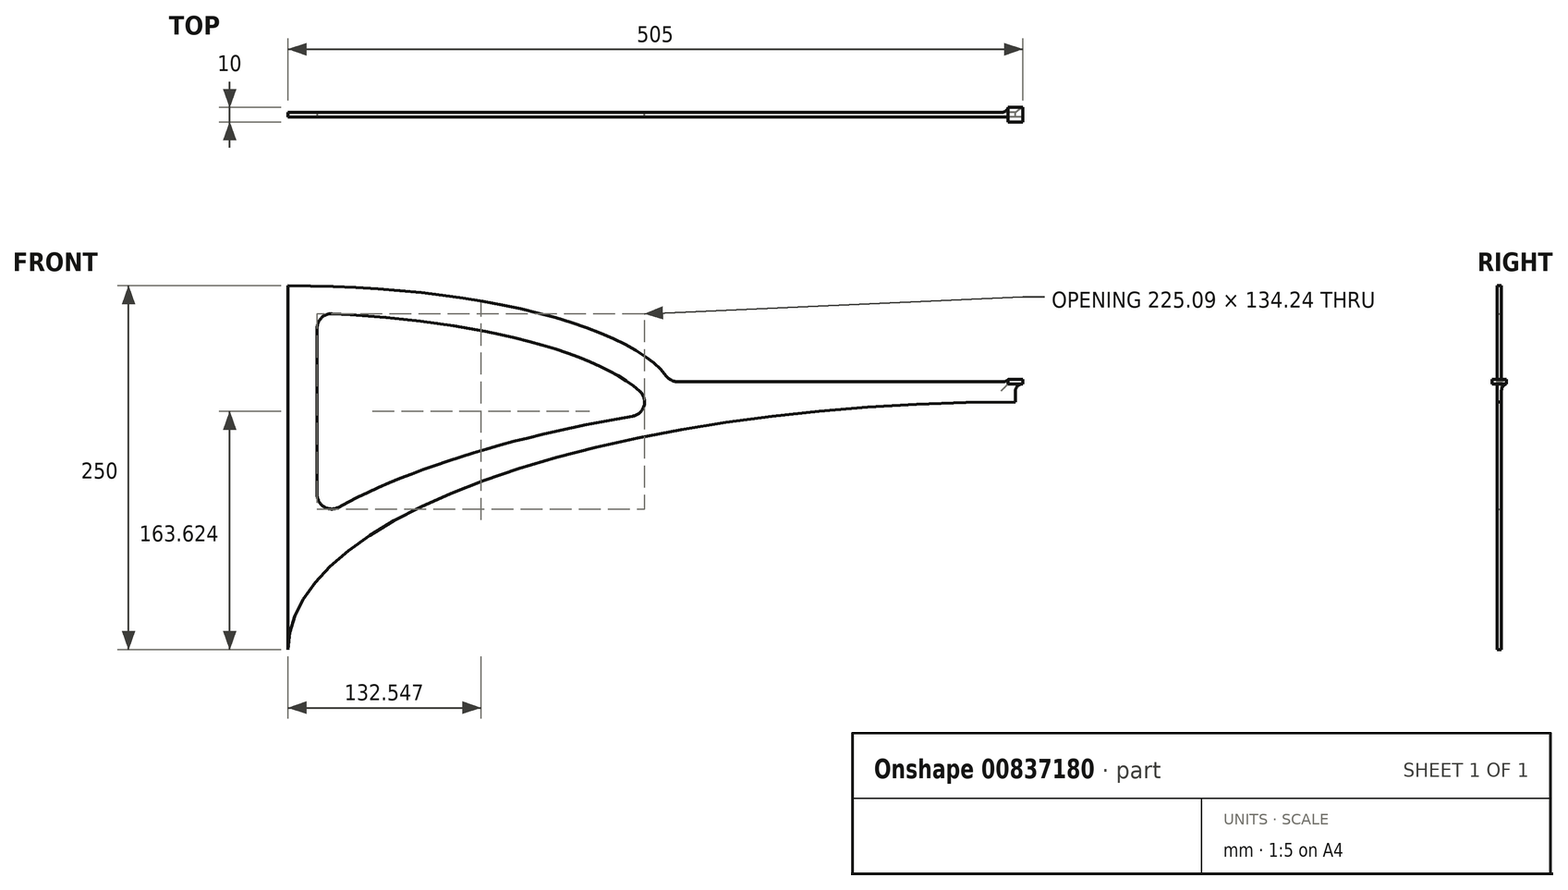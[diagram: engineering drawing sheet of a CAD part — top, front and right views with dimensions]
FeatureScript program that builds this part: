
annotation { "Feature Type Name" : "Feature", "Feature Type Description" : "" }
export const myFeature = defineFeature(function(context is Context, id is Id, definition is map)
    precondition{}
    {
        {
            var Q0;
            Q0=qCreatedBy(makeId("Front.planeOp"),FACE);
            var sketch = newSketch(context, id + "F0", { "sketchPlane" : qUnion([Q0])});
            skLineSegment(sketch, "E0", {"start": v(0, 0) * mm, "end": v(20, 0) * mm});
            skLineSegment(sketch, "E1", {"start": v(0, 0) * mm, "end": v(0, -170) * mm});
            skLineSegment(sketch, "E2", {"start": v(0, 0) * mm, "end": v(0, 80) * mm});
            skEllipticalArc(sketch, "E3", {});
            skEllipticalArc(sketch, "E4", {});
            skLineSegment(sketch, "E5", {"start": v(0, 80) * mm, "end": v(20, 80) * mm});
            skLineSegment(sketch, "E6", {"start": v(20, 80) * mm, "end": v(20, 79.77) * mm});
            skEllipticalArc(sketch, "E7", {});
            skEllipticalArc(sketch, "E8.trimOffspring", {});
            skLineSegment(sketch, "E9.trimOffspring", {"start": v(20, 61.17) * mm, "end": v(20, -80.93) * mm});
            skLineSegment(sketch, "E10", {"start": v(495, 14) * mm, "end": v(262.66, 14) * mm});
            skLineSegment(sketch, "E11", {"start": v(500, 12.5) * mm, "end": v(500, 0) * mm});
            skLineSegment(sketch, "E12", {"start": v(505, 15.5) * mm, "end": v(505, 12.5) * mm});
            skLineSegment(sketch, "E13", {"start": v(505, 12.5) * mm, "end": v(495, 12.5) * mm});
            skLineSegment(sketch, "E14", {"start": v(495, 12.5) * mm, "end": v(495, 15.5) * mm});
            skLineSegment(sketch, "E15", {"start": v(505, 15.5) * mm, "end": v(495, 15.5) * mm});
            const initialGuessF0  = {"E3": [0.5, -0.17, -1, 0, 0.5, 0.17, 4.71238898038469, 0], "E4": [0, 0, 1, 0, 0.2667732536792755, 0.08, 0.175905768163716, 1.5707963267948966], "E7": [-0.010746347717940807, -0.01829361915588379, 1, 0, 0.2667732536792755, 0.08, 0.1402518701744699, 1.4552868981173144], "E8.trimOffspring": [0.4594820141792296, -0.162, -1, 0, 0.5, 0.17, 5.137200659340416, 5.78607445460218]};
            skSetInitialGuess(sketch, initialGuessF0);
            skSolve(sketch);
        }
        {
            var Q0;
            Q0=makeQuery(id+"F0.imprint","IMPRINT",FACE,{"disambiguationData":[TD([[makeQuery(id+"F0.imprint","IMPRINT",EDGE,{"derivedFrom":sQuery(id+"F0.wireOp",EDGE,"E1")}),1.0]])]});
            extrude(context, id + "F1", {"entities" : qUnion([Q0]), "depth" : 1.5 * mm, "offsetDistance" : 25 * mm});
        }
        {
            var Q0;
            {var subQ5=sQuery(id+"F0.wireOp",EDGE,"E12");Q0=makeQuery(id+"F0.imprint","IMPRINT",FACE,{"disambiguationData":[TD([[makeQuery(id+"F0.imprint","IMPRINT",EDGE,{"derivedFrom":subQ5}),-1.0]])]});}
            extrude(context, id + "F2", {"entities" : qUnion([Q0]), "operationType" : NewBodyOperationType.ADD, "depth" : 5 * mm, "offsetDistance" : 25 * mm});
        }
        {
            var Q0;
            Q0=makeQuery(id+"F0.imprint","IMPRINT",FACE,{"disambiguationData":[TD([[makeQuery(id+"F0.imprint","IMPRINT",EDGE,{"derivedFrom":sQuery(id+"F0.wireOp",EDGE,"E1")}),1.0]])]});
            extrude(context, id + "F3", {"entities" : qUnion([Q0]), "operationType" : NewBodyOperationType.ADD, "oppositeDirection" : true, "depth" : 1.5 * mm, "offsetDistance" : 25 * mm});
        }
        {
            var Q0;
            {var subQ5=sQuery(id+"F0.wireOp",EDGE,"E12");Q0=makeQuery(id+"F0.imprint","IMPRINT",FACE,{"disambiguationData":[TD([[makeQuery(id+"F0.imprint","IMPRINT",EDGE,{"derivedFrom":subQ5}),-1.0]])]});}
            extrude(context, id + "F4", {"entities" : qUnion([Q0]), "operationType" : NewBodyOperationType.ADD, "oppositeDirection" : true, "depth" : 5 * mm, "offsetDistance" : 25 * mm});
        }
        {
            var Q0;
            {var subQ0=sQuery(id+"F0.wireOp",EDGE,"E10");var subQ1=sQuery(id+"F0.wireOp",EDGE,"E4");Q0=makeQuery(id+"F3.boolean.opBoolean","MERGE",EDGE,{"derivedFrom":[makeQuery(id+"F1.opExtrude","SWEPT_EDGE",EDGE,{"disambiguationData":[OSD([subQ1,subQ0])]}),makeQuery(id+"F3.opExtrude","SWEPT_EDGE",EDGE,{"disambiguationData":[OSD([subQ1,subQ0])]})]});}
            var Q1;
            {var subQ0=sQuery(id+"F0.wireOp",EDGE,"E8.trimOffspring");var subQ1=sQuery(id+"F0.wireOp",EDGE,"E7");Q1=makeQuery(id+"F3.boolean.opBoolean","MERGE",EDGE,{"derivedFrom":[makeQuery(id+"F1.opExtrude","SWEPT_EDGE",EDGE,{"disambiguationData":[OSD([subQ1,subQ0])]}),makeQuery(id+"F3.opExtrude","SWEPT_EDGE",EDGE,{"disambiguationData":[OSD([subQ1,subQ0])]})]});}
            var Q2;
            {var subQ0=sQuery(id+"F0.wireOp",EDGE,"E9.trimOffspring");var subQ1=sQuery(id+"F0.wireOp",EDGE,"E8.trimOffspring");Q2=makeQuery(id+"F3.boolean.opBoolean","MERGE",EDGE,{"derivedFrom":[makeQuery(id+"F1.opExtrude","SWEPT_EDGE",EDGE,{"disambiguationData":[OSD([subQ1,subQ0])]}),makeQuery(id+"F3.opExtrude","SWEPT_EDGE",EDGE,{"disambiguationData":[OSD([subQ1,subQ0])]})]});}
            var Q3;
            {var subQ0=sQuery(id+"F0.wireOp",EDGE,"E9.trimOffspring");var subQ1=sQuery(id+"F0.wireOp",EDGE,"E7");Q3=makeQuery(id+"F3.boolean.opBoolean","MERGE",EDGE,{"derivedFrom":[makeQuery(id+"F1.opExtrude","SWEPT_EDGE",EDGE,{"disambiguationData":[OSD([subQ1,subQ0])]}),makeQuery(id+"F3.opExtrude","SWEPT_EDGE",EDGE,{"disambiguationData":[OSD([subQ1,subQ0])]})]});}
            fillet(context, id + "F5", {"entities" : qUnion([Q0, Q1, Q2, Q3]), "radius" : 10 * mm, "tangentPropagation" : true, "allowEdgeOverflow" : false});
        }
        {
            var Q0;
            {var subQ0=sQuery(id+"F0.wireOp",EDGE,"E14");var subQ1=sQuery(id+"F0.wireOp",EDGE,"E10");Q0=makeQuery(id+"F4.boolean.opBoolean","MERGE",EDGE,{"derivedFrom":[makeQuery(id+"F1.opExtrude","SWEPT_EDGE",EDGE,{"disambiguationData":[OSD([subQ1,subQ0])]}),makeQuery(id+"F3.opExtrude","SWEPT_EDGE",EDGE,{"disambiguationData":[OSD([subQ1,subQ0])]})]});}
            fillet(context, id + "F6", {"entities" : qUnion([Q0]), "radius" : 5 * mm, "tangentPropagation" : true, "allowEdgeOverflow" : false});
        }
        {
            var Q0;
            Q0=makeQuery(id+"F1.opExtrude","CAP_EDGE",EDGE,{"disambiguationData":[OSD([sQuery(id+"F0.wireOp",EDGE,"E14")])],"isStart":false});
            var Q1;
            Q1=makeQuery(id+"F3.opExtrude","CAP_EDGE",EDGE,{"disambiguationData":[OSD([sQuery(id+"F0.wireOp",EDGE,"E14")])],"isStart":false});
            fillet(context, id + "F7", {"entities" : qUnion([Q0, Q1]), "radius" : 5 * mm, "tangentPropagation" : true, "allowEdgeOverflow" : false});
        }
        {
            var Q0;
            {var subQ0=sQuery(id+"F0.wireOp",EDGE,"E13");var subQ1=sQuery(id+"F0.wireOp",EDGE,"E11");Q0=makeQuery(id+"F4.boolean.opBoolean","MERGE",EDGE,{"derivedFrom":[makeQuery(id+"F1.opExtrude","SWEPT_EDGE",EDGE,{"disambiguationData":[OSD([subQ1,subQ0])]}),makeQuery(id+"F3.opExtrude","SWEPT_EDGE",EDGE,{"disambiguationData":[OSD([subQ1,subQ0])]})]});}
            var Q1;
            Q1=makeQuery(id+"F3.opExtrude","CAP_EDGE",EDGE,{"disambiguationData":[OSD([sQuery(id+"F0.wireOp",EDGE,"E13")])],"isStart":false});
            var Q2;
            Q2=makeQuery(id+"F1.opExtrude","CAP_EDGE",EDGE,{"disambiguationData":[OSD([sQuery(id+"F0.wireOp",EDGE,"E13")])],"isStart":false});
            fillet(context, id + "F8", {"entities" : qUnion([Q0, Q1, Q2]), "radius" : 5 * mm, "tangentPropagation" : true, "allowEdgeOverflow" : false});
        }
    });
